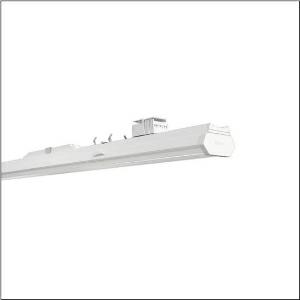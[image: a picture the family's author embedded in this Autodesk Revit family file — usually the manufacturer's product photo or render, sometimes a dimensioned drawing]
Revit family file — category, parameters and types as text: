
# Revit family: licross_r__11_protected_mo_51tp12dn49xf_8d80
name_source: partatom
category: Lighting Fixtures
units: mm (PartAtom-declared; Revit-internal decimal feet)

## family parameters
Cut with Voids When Loaded = No
Host = Face
Light Source = No
Part Type = Normal
Room Calculation Point = No
Round Connector Dimension = Use Diameter
Shared = No

## types (1)
- --- (1 x LED, 9020 lm, 56.2 W, 4000K)
    Apparent Load = 56 VA
    CIE Flux Codes = 73 92 98 99 100
    Color Rendering = 80
    Color Temperature = 4000K
    Default Elevation = 1800 mm
    Description = Licross® 11 Protected MOluminaire insert, length: 1.500mm, width: 90mm, height: 101mm, LED rated luminous flux: 9.020lm, light colour: 840, control gear: DALI 2, control gear: ECG DALI, with plug, 5-pole, with phase selection, mains connection: 220..240V, AC, 50/60Hz, halogen-free wiring, primary optical cover: cover, of PMMA, light emission: direct with ceiling illumination distribution, protection rating (complete): IP64, insulation class (complete): insulation class I (protective earthing), certification: CE, ENEC, VDE, protection symbol: D if used in an environment with conductive dust loads with corresponding accessories, permissible ambient temperature for indoor applications: -25..+40°C, reducing of maximum allowable ambient temperature of 5°C with ceiling mounting, corresponds to IFS (International Featured Standards) requirements for safety and quality in the food industry, packaging unit: 1 piece
    Height = 92 mm
    Lamp = 1 x LED
    Lamp Light Flux = 9020 lm
    Lamp Power = 56.2 W
    Lamp count = 1
    Length = 1500 mm
    Luminous efficacy = 161 lm/W
    Manufacturer = Siteco
    ModVariant = No
    Model = 51TP12DN49XF
    Mounting Place = Ceiling
    Mounting Type = Pendant
    Number of Poles = 1
    OnlyDefault = Yes
    Power Factor = 1
    Product Name = Licross® 11 Protected MO
    Product group = luminaire insert
    ProductGroupID = 902
    Protection Class = Protection class I
    Protection Degree = IP 64
    RLX_Detail_Level = 1
    RlxData = <blob elided: 24057 chars, md5=c62dcd89>
    Socket = socket
    Standby Power = 0 W
    System Light Flux = 9020 lm
    System Power = 56 W
    Type Comments = factory setting: luminous flux: 100 % | dim-lin: 254 | 370 mA
    Type Image = l_1256148.jpg
    URL = http://relux.com
    VarID = @adj_137869
    Voltage = 0 V
    Weight = 0.00 kg
    Width = 88 mm

## geometry (parser evidence)
native form markers: Blend x4, Sweep x12
no freeform markers — native parametric forms only
